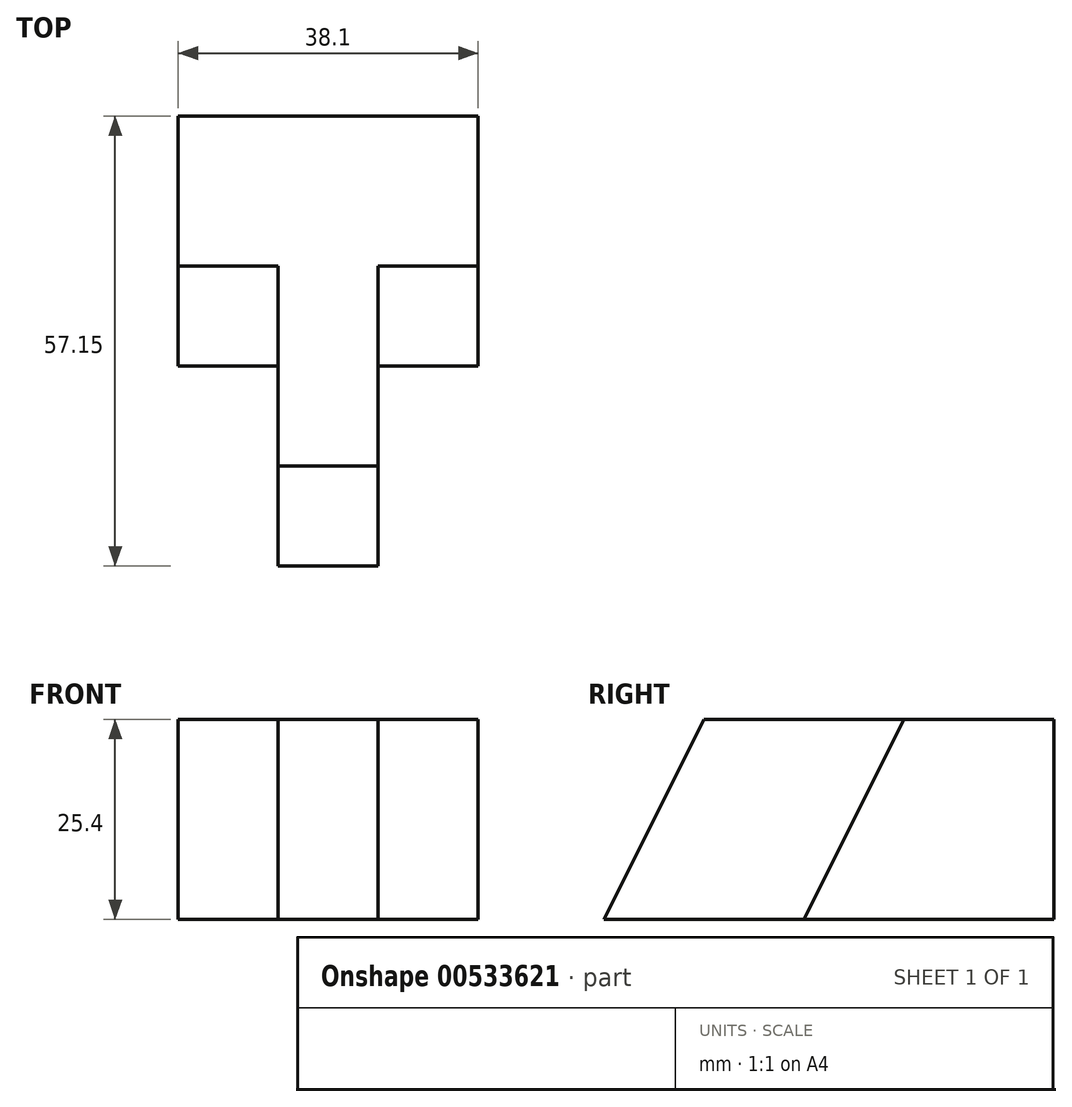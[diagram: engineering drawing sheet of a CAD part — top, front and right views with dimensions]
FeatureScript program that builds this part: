
annotation { "Feature Type Name" : "Feature", "Feature Type Description" : "" }
export const myFeature = defineFeature(function(context is Context, id is Id, definition is map)
    precondition{}
    {
        {
            var Q0;
            Q0=qCreatedBy(makeId("Front.planeOp"),FACE);
            var sketch = newSketch(context, id + "F0", { "sketchPlane" : qUnion([Q0])});
            skLineSegment(sketch, "E0", {"start": v(0, 0) * mm, "end": v(-38.1, 0) * mm});
            skLineSegment(sketch, "E1", {"start": v(-38.1, 0) * mm, "end": v(-38.1, 25.4) * mm});
            skLineSegment(sketch, "E2", {"start": v(-38.1, 25.4) * mm, "end": v(0, 25.4) * mm});
            skLineSegment(sketch, "E3", {"start": v(0, 25.4) * mm, "end": v(0, 0) * mm});
            skSolve(sketch);
        }
        {
            var Q0;
            Q0 = qSketchRegion(id + "F0", true);
            extrude(context, id + "F1", {"entities" : qUnion([Q0]), "depth" : 19.05 * mm, "offsetDistance" : 25.4 * mm});
        }
        {
            var Q0;
            Q0=makeQuery(id+"F1.opExtrude","CAP_FACE",FACE,{"disambiguationData":[OSD([sQuery(id+"F0.wireOp",EDGE,"E0"),sQuery(id+"F0.wireOp",EDGE,"E1"),sQuery(id+"F0.wireOp",EDGE,"E2"),sQuery(id+"F0.wireOp",EDGE,"E3")])],"isStart":false});
            var sketch = newSketch(context, id + "F2", { "sketchPlane" : qUnion([Q0])});
            skLineSegment(sketch, "E4", {"start": v(-25.4, 25.4) * mm, "end": v(-25.4, 0) * mm});
            skLineSegment(sketch, "E5", {"start": v(-25.4, 0) * mm, "end": v(-12.7, 0) * mm});
            skLineSegment(sketch, "E6", {"start": v(-12.7, 0) * mm, "end": v(-12.7, 25.4) * mm});
            skLineSegment(sketch, "E7", {"start": v(-12.7, 25.4) * mm, "end": v(-25.4, 25.4) * mm});
            skSolve(sketch);
        }
        {
            var Q0;
            Q0 = qSketchRegion(id + "F2", true);
            extrude(context, id + "F3", {"entities" : qUnion([Q0]), "operationType" : NewBodyOperationType.ADD, "depth" : 38.1 * mm, "offsetDistance" : 25.4 * mm});
        }
        {
            var Q0;
            Q0=makeQuery(id+"F3.opExtrude","SWEPT_FACE",FACE,{"disambiguationData":[OSD([sQuery(id+"F2.wireOp",EDGE,"E4")])]});
            var sketch = newSketch(context, id + "F4", { "sketchPlane" : qUnion([Q0])});
            skLineSegment(sketch, "E8", {"start": v(57.15, 0) * mm, "end": v(44.45, 25.4) * mm});
            skSolve(sketch);
        }
        {
            var Q0;
            Q0 = qSketchRegion(id + "F4", true);
            var Q1;
            {var subQ0=sQuery(id+"F4.wireOp",EDGE,"E8");Q1=makeQuery(id+"F4.imprint","IMPRINT",FACE,{"disambiguationData":[TD([[makeQuery(id+"F4.imprint","IMPRINT",EDGE,{"derivedFrom":subQ0}),-1.0]])]});}
            extrude(context, id + "F5", {"entities" : qUnion([Q0, Q1]), "operationType" : NewBodyOperationType.REMOVE, "oppositeDirection" : true, "depth" : 25.4 * mm, "offsetDistance" : 25.4 * mm});
        }
        {
            var Q0;
            Q0=makeQuery(id+"F3.opExtrude","SWEPT_FACE",FACE,{"disambiguationData":[OSD([sQuery(id+"F2.wireOp",EDGE,"E4")])]});
            var sketch = newSketch(context, id + "F6", { "sketchPlane" : qUnion([Q0])});
            skLineSegment(sketch, "E9", {"start": v(31.75, 0) * mm, "end": v(19.05, 25.4) * mm});
            skLineSegment(sketch, "E10", {"start": v(19.05, 25.4) * mm, "end": v(19.05, 0) * mm});
            skLineSegment(sketch, "E11", {"start": v(19.05, 0) * mm, "end": v(31.75, 0) * mm});
            skSolve(sketch);
        }
        {
            var Q0;
            Q0 = qSketchRegion(id + "F6", true);
            extrude(context, id + "F7", {"entities" : qUnion([Q0]), "operationType" : NewBodyOperationType.ADD, "depth" : 12.7 * mm, "offsetDistance" : 25.4 * mm});
        }
        {
            var Q0;
            Q0=makeQuery(id+"F3.opExtrude","SWEPT_FACE",FACE,{"disambiguationData":[OSD([sQuery(id+"F2.wireOp",EDGE,"E6")])]});
            var sketch = newSketch(context, id + "F8", { "sketchPlane" : qUnion([Q0])});
            skLineSegment(sketch, "E12", {"start": v(-31.75, 0) * mm, "end": v(-19.05, 25.4) * mm});
            skLineSegment(sketch, "E13", {"start": v(-19.05, 25.4) * mm, "end": v(-19.05, 0) * mm});
            skLineSegment(sketch, "E14", {"start": v(-19.05, 0) * mm, "end": v(-31.75, 0) * mm});
            skSolve(sketch);
        }
        {
            var Q0;
            Q0 = qSketchRegion(id + "F8", true);
            extrude(context, id + "F9", {"entities" : qUnion([Q0]), "operationType" : NewBodyOperationType.ADD, "depth" : 12.7 * mm, "offsetDistance" : 25.4 * mm});
        }
    });
